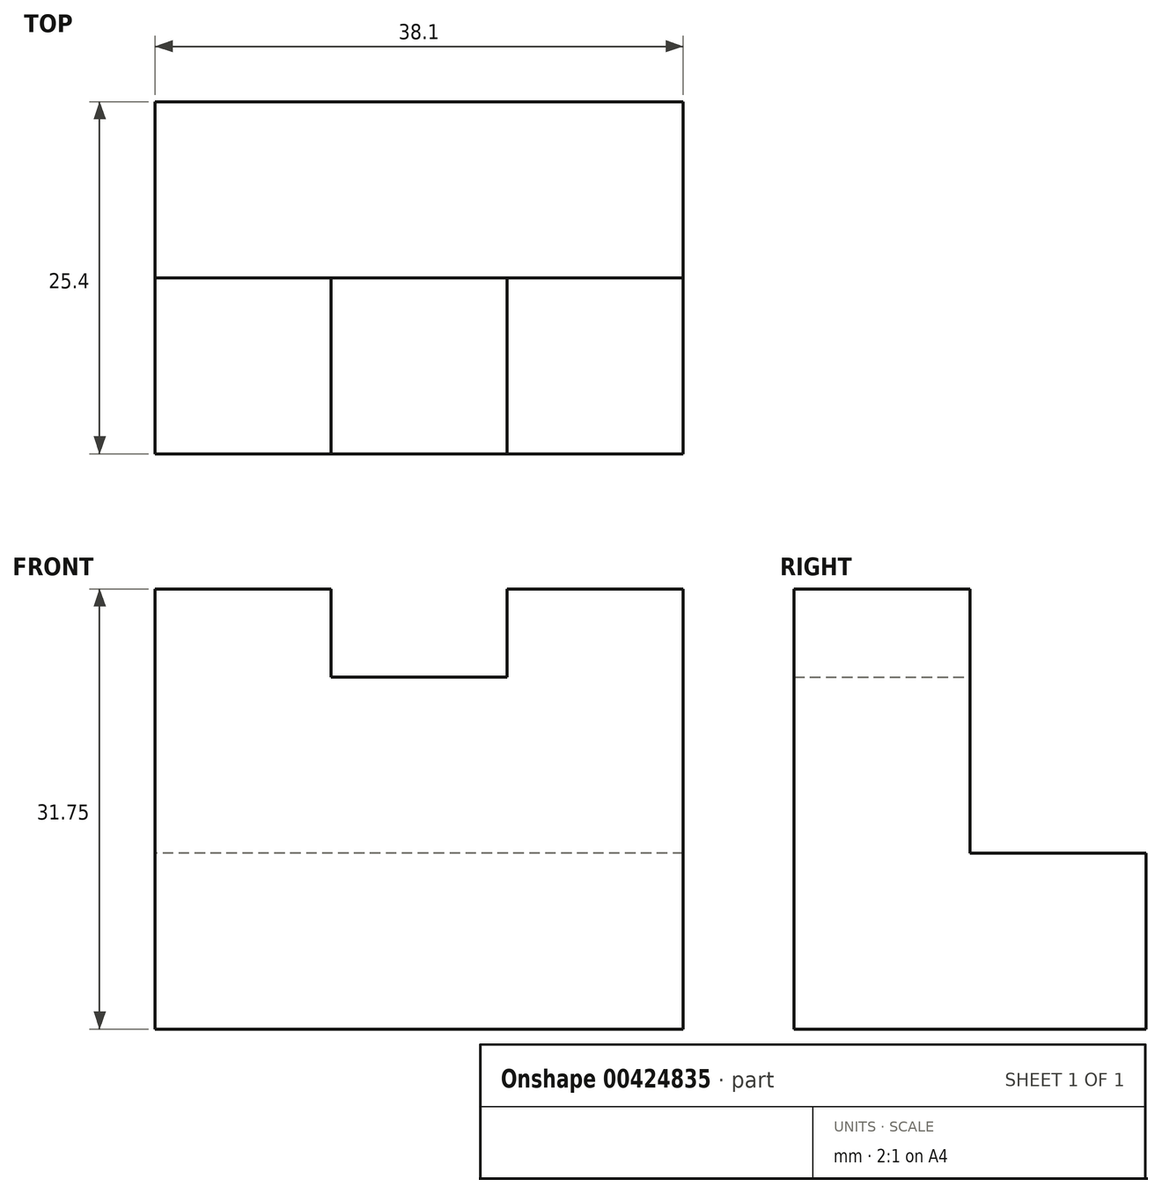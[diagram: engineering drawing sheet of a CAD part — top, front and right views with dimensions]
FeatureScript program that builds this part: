
annotation { "Feature Type Name" : "Feature", "Feature Type Description" : "" }
export const myFeature = defineFeature(function(context is Context, id is Id, definition is map)
    precondition{}
    {
        {
            var Q0;
            Q0=qCreatedBy(makeId("Front.planeOp"),FACE);
            var sketch = newSketch(context, id + "F0", { "sketchPlane" : qUnion([Q0])});
            skLineSegment(sketch, "E0", {"start": v(0, 0) * mm, "end": v(38.1, 0) * mm});
            skLineSegment(sketch, "E1", {"start": v(38.1, 0) * mm, "end": v(38.1, 12.7) * mm});
            skLineSegment(sketch, "E2", {"start": v(38.1, 12.7) * mm, "end": v(0, 12.7) * mm});
            skLineSegment(sketch, "E3", {"start": v(0, 12.7) * mm, "end": v(0, 0) * mm});
            skLineSegment(sketch, "E4", {"start": v(0, 12.7) * mm, "end": v(0, 31.75) * mm});
            skLineSegment(sketch, "E5", {"start": v(0, 31.75) * mm, "end": v(12.7, 31.75) * mm});
            skLineSegment(sketch, "E6", {"start": v(12.7, 31.75) * mm, "end": v(12.7, 25.4) * mm});
            skLineSegment(sketch, "E7", {"start": v(12.7, 25.4) * mm, "end": v(25.4, 25.4) * mm});
            skLineSegment(sketch, "E8", {"start": v(25.4, 25.4) * mm, "end": v(25.4, 31.75) * mm});
            skLineSegment(sketch, "E9", {"start": v(25.4, 31.75) * mm, "end": v(38.1, 31.75) * mm});
            skLineSegment(sketch, "E10", {"start": v(38.1, 31.75) * mm, "end": v(38.1, 12.7) * mm});
            skSolve(sketch);
        }
        {
            var Q0;
            Q0 = qSketchRegion(id + "F0", true);
            extrude(context, id + "F1", {"entities" : qUnion([Q0]), "depth" : 12.7 * mm});
        }
        {
            var Q0;
            Q0=qCreatedBy(makeId("Right.planeOp"),FACE);
            var sketch = newSketch(context, id + "F2", { "sketchPlane" : qUnion([Q0])});
            skLineSegment(sketch, "E11", {"start": v(0, 0) * mm, "end": v(12.7, 0) * mm});
            skLineSegment(sketch, "E12", {"start": v(12.7, 0) * mm, "end": v(12.7, 12.7) * mm});
            skLineSegment(sketch, "E13", {"start": v(12.7, 12.7) * mm, "end": v(0, 12.7) * mm});
            skLineSegment(sketch, "E14", {"start": v(0, 12.7) * mm, "end": v(0, 0) * mm});
            skSolve(sketch);
        }
        {
            var Q0;
            Q0 = qSketchRegion(id + "F2", true);
            extrude(context, id + "F3", {"entities" : qUnion([Q0]), "operationType" : NewBodyOperationType.ADD, "depth" : 38.1 * mm});
        }
    });
